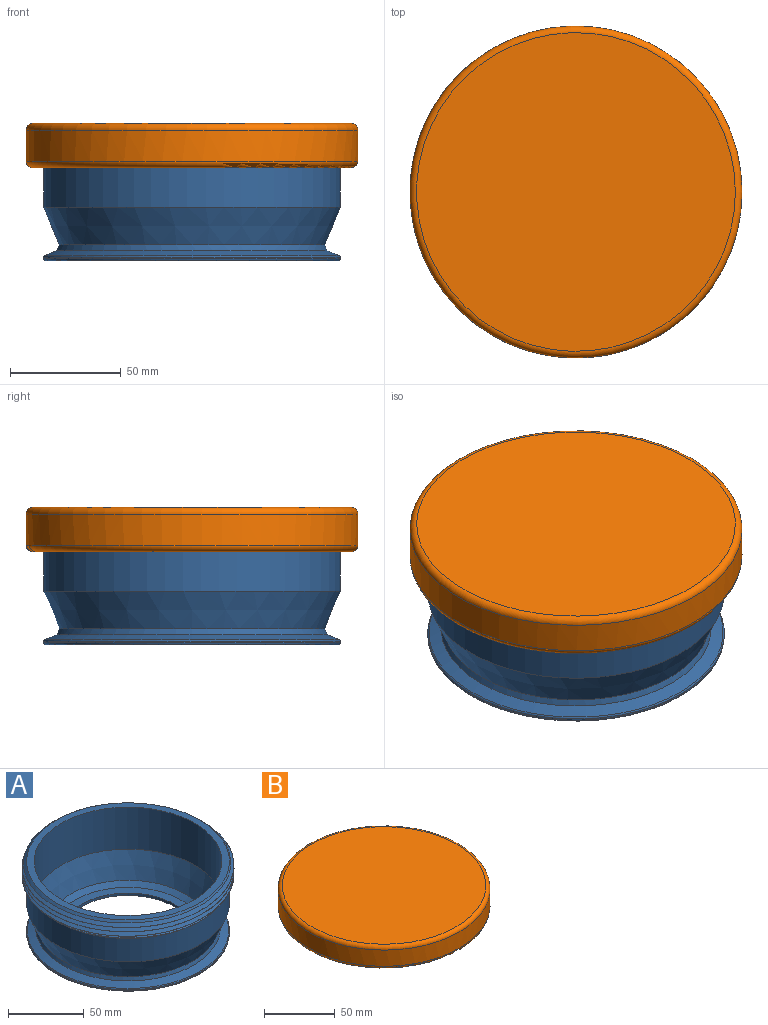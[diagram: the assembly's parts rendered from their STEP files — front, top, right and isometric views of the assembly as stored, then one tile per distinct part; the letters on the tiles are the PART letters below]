
ASSEMBLY  parts=2 mates=1
PART A: 19 faces, bbox 145x161.7x59.9 mm
  f0: plane 134x134mm, normal (0,0,1), area 2026.3mm2, adj f7,f13
  f1: cylinder r=70mm len=140mm, axis (0,0,1), area 39.9mm2, adj f12,f13,f14,f15
  f2: cylinder r=67mm len=134mm, axis (0,0,1), area 7971.1mm2, adj f3,f12
  f3: cone r=59.18mm half-angle=22.6deg, axis (0,0,1), area 7328.7mm2, adj f2,f16
  f4: cone r=67mm half-angle=67.4deg, axis (0,0,-1), area 2377.2mm2, adj f16,f17
  f5: cylinder r=67mm len=134mm, axis (0,0,1), area 280.4mm2, adj f17,f18
  f6: plane 132.4x132.4mm, normal (0,0,-1), area 7959mm2, adj f11,f18
  f7: cylinder r=62mm len=124mm, axis (0,0,-1), area 13219.8mm2, adj f0,f8
  f8: cone r=62mm half-angle=23.3deg, axis (0,0,1), area 7640.5mm2, adj f7,f9
  f9: cone r=53.69mm half-angle=56.6deg, axis (0,0,1), area 1624.7mm2, adj f8,f10
  f10: plane 99x99mm, normal (0,0,1), area 1888.9mm2, adj f9,f11
  f11: cylinder r=43mm len=86mm, axis (0,0,-1), area 540.4mm2, adj f6,f10
  f12: cone r=70mm half-angle=45deg, axis (0,0,1), area 916.3mm2, adj f1,f2,f14,f15
  f13: cone r=67mm half-angle=45deg, axis (0,0,-1), area 917.7mm2, adj f0,f1,f14,f15
  f14: bspline ~161.66x140mm, area 5100.4mm2, adj f1,f12,f13,f15
  f15: bspline ~161.66x140mm, area 5101.7mm2, adj f1,f12,f13,f14
  f16: cone r=59.95mm half-angle=22.4deg, axis (0,0,-1), area 1075mm2, adj f3,f4
  f17: torus R=66.2mm, axis (0,0,-1), area 395.4mm2, adj f4,f5
  f18: torus R=66.2mm, axis (0,0,1), area 526.7mm2, adj f5,f6
PART B: 19 faces, bbox 162.4x164x20.3 mm
  f0: plane 143x143mm, normal (0,0,-1), area 16050.9mm2, adj f9,f11,f12,f13
  f1: plane 144x144mm, normal (0,0,1), area 16286mm2, adj f17
  f2: cylinder r=75mm len=150mm, axis (0,0,1), area 6597.3mm2, adj f17,f18
  f3: plane 144x144mm, normal (0,0,-1), area 449.2mm2, adj f4,f18
  f4: cylinder r=71mm len=142mm, axis (0,0,1), area 781mm2, adj f3,f7,f10,f14,f16
  f5: cylinder r=71mm len=142mm, axis (0,0,1), area 92.6mm2, adj f6,f8,f12,f14
  f6: cylinder r=71mm len=142mm, axis (0,0,1), area 118.8mm2, adj f5,f7,f12,f14
  f7: cylinder r=71mm len=142mm, axis (0,0,1), area 119.5mm2, adj f4,f6,f12,f14,f15
  f8: plane 143x143mm, normal (0,0,1), area 223.8mm2, adj f5,f9,f13
  f9: cylinder r=71.5mm len=143mm, axis (0,0,1), area 1316.8mm2, adj f0,f8
  f10: plane 0.47x0.41mm, normal (0,-1,0), area 0.1mm2, adj f4,f15,f16
  f11: plane 2.94x2.79mm, normal (0.99,-0.1,0), area 4.4mm2, adj f0,f12,f13,f14
  f12: bspline ~163.97x142mm, area 5264.2mm2, adj f0,f5,f6,f7,f11,f13,f14,f15
  f13: cylinder r=71mm len=142mm, axis (0,0,1), area 662.1mm2, adj f0,f8,f11,f12
  f14: bspline ~163.97x142mm, area 5279.2mm2, adj f4,f5,f6,f7,f11,f12,f16
  f15: bspline ~4.68x3.39mm, area 4mm2, adj f7,f10,f12,f16
  f16: bspline ~4.68x3.39mm, area 4.2mm2, adj f4,f10,f12,f14,f15
  f17: torus R=72mm, axis (0,0,1), area 2188.4mm2, adj f1,f2
  f18: torus R=72mm, axis (0,0,-1), area 2188.4mm2, adj f2,f3
PLACE A t=(-39.72,-6.6,-6.78)mm fixed
PLACE B rot(axis=(0,0,-1),169.5deg) t=(-39.71,-6.56,76.59)mm
MATE revolute B.f0 <-> A.f1  axis (0,0,-1) through (-39.72,-6.6,51.22)mm
